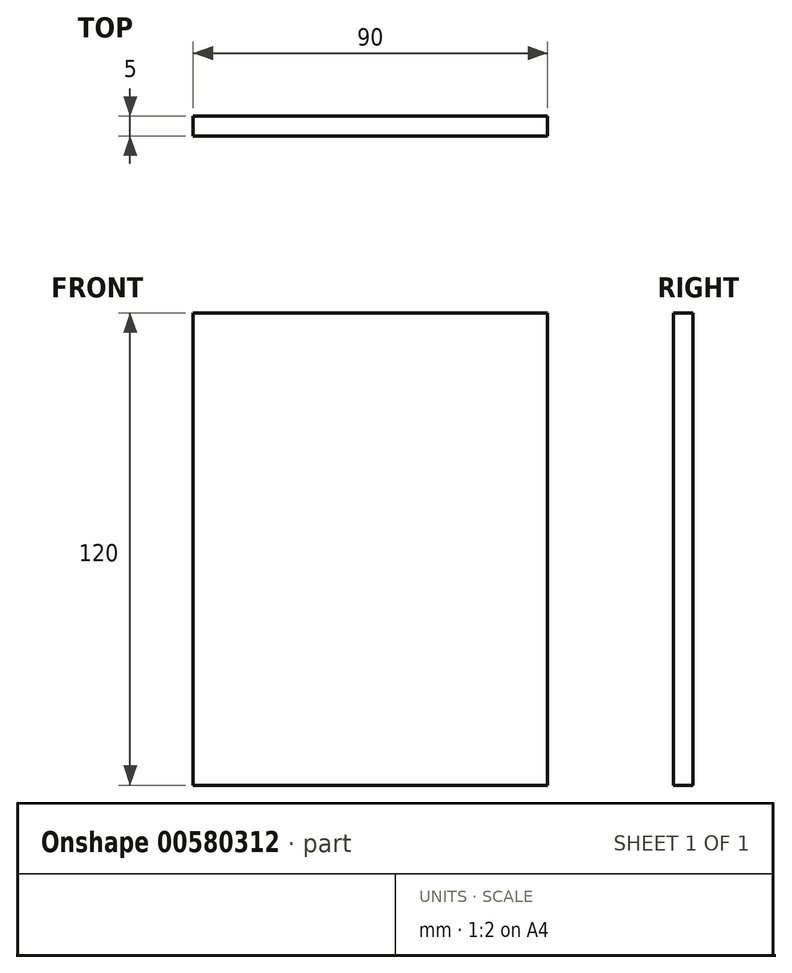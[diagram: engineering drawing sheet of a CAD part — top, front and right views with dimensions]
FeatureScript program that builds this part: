
annotation { "Feature Type Name" : "Feature", "Feature Type Description" : "" }
export const myFeature = defineFeature(function(context is Context, id is Id, definition is map)
    precondition{}
    {
        {
            var Q0;
            Q0=qCreatedBy(makeId("Front.planeOp"),FACE);
            var sketch = newSketch(context, id + "F0", { "sketchPlane" : qUnion([Q0])});
            skLineSegment(sketch, "E0.bottom", {"start": v(45, 0) * mm, "end": v(-45, 0) * mm});
            skLineSegment(sketch, "E0.top", {"start": v(45, -120) * mm, "end": v(-45, -120) * mm});
            skLineSegment(sketch, "E0.left", {"start": v(45, 0) * mm, "end": v(45, -120) * mm});
            skLineSegment(sketch, "E0.right", {"start": v(-45, 0) * mm, "end": v(-45, -120) * mm});
            skSolve(sketch);
        }
        {
            var Q0;
            Q0=makeQuery(id+"F0.imprint","IMPRINT",FACE,{"disambiguationData":[TD([[makeQuery(id+"F0.imprint","IMPRINT",EDGE,{"derivedFrom":sQuery(id+"F0.wireOp",EDGE,"E0.bottom")}),1.0]])]});
            extrude(context, id + "F1", {"entities" : qUnion([Q0]), "depth" : 5 * mm, "offsetDistance" : 25 * mm});
        }
    });
